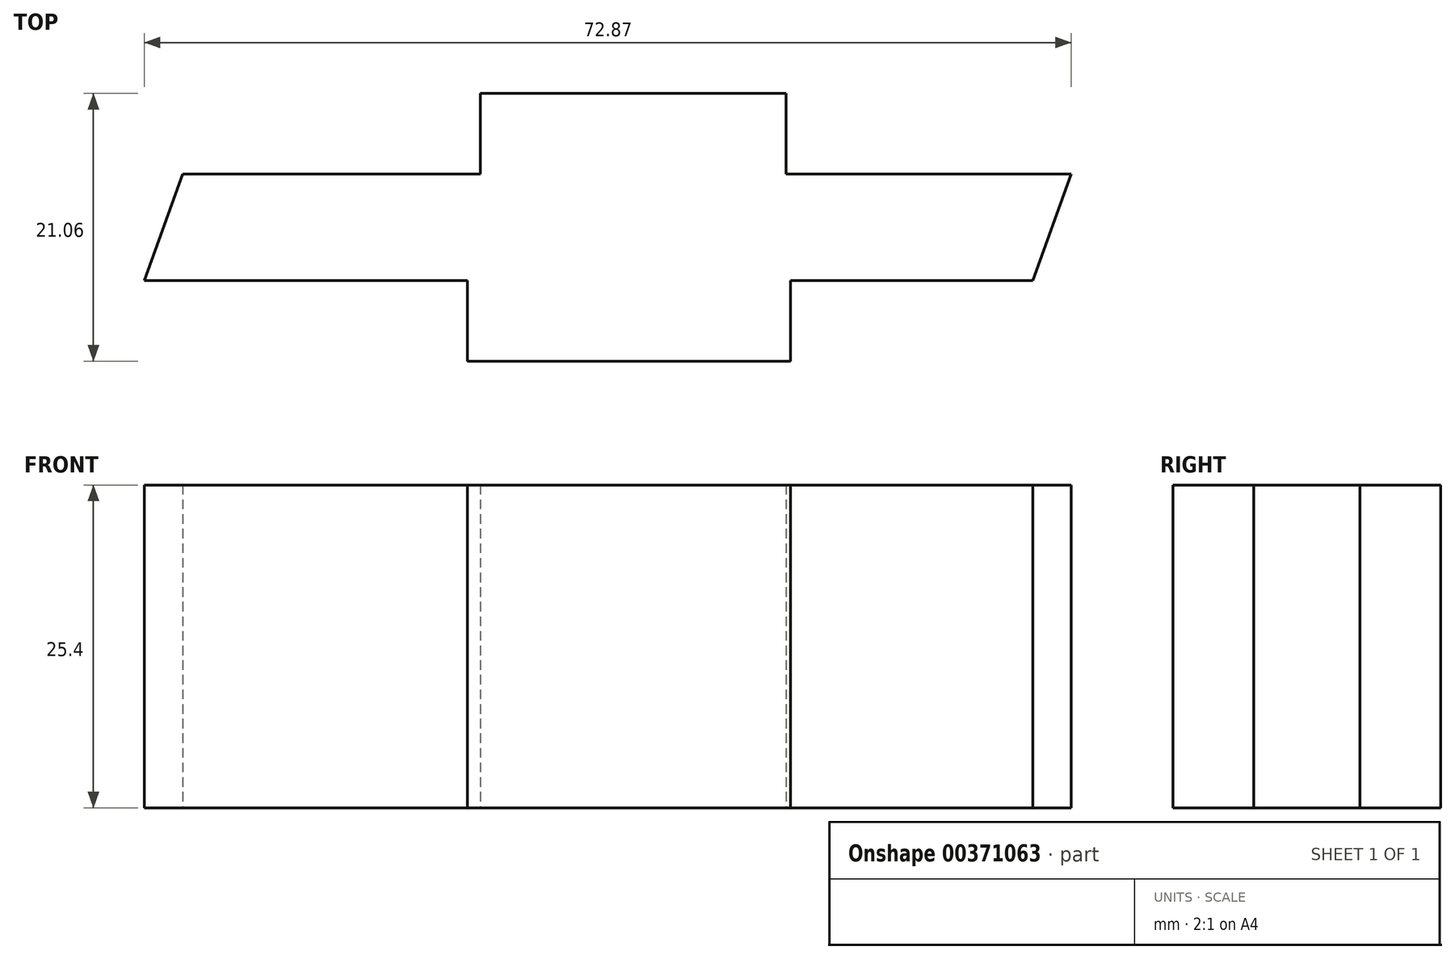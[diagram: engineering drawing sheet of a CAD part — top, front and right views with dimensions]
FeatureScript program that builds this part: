
annotation { "Feature Type Name" : "Feature", "Feature Type Description" : "" }
export const myFeature = defineFeature(function(context is Context, id is Id, definition is map)
    precondition{}
    {
        {
            var Q0;
            Q0=qCreatedBy(makeId("Top.planeOp"),FACE);
            var sketch = newSketch(context, id + "F0", { "sketchPlane" : qUnion([Q0])});
            skLineSegment(sketch, "E0", {"start": v(-22.5, 0) * mm, "end": v(2.9, 0) * mm});
            skLineSegment(sketch, "E1", {"start": v(2.9, 0) * mm, "end": v(2.9, 6.35) * mm});
            skLineSegment(sketch, "E2", {"start": v(2.9, 6.35) * mm, "end": v(21.95, 6.35) * mm});
            skLineSegment(sketch, "E3", {"start": v(-22.5, 0) * mm, "end": v(-22.5, 6.35) * mm});
            skLineSegment(sketch, "E4", {"start": v(-22.5, 6.35) * mm, "end": v(-47.9, 6.35) * mm});
            skLineSegment(sketch, "E5", {"start": v(21.95, 6.35) * mm, "end": v(24.97, 14.71) * mm});
            skLineSegment(sketch, "E6", {"start": v(24.97, 14.71) * mm, "end": v(2.56, 14.71) * mm});
            skLineSegment(sketch, "E7", {"start": v(2.56, 14.71) * mm, "end": v(2.56, 21.06) * mm});
            skLineSegment(sketch, "E8", {"start": v(2.56, 21.06) * mm, "end": v(-21.5, 21.06) * mm});
            skLineSegment(sketch, "E9", {"start": v(-21.5, 21.06) * mm, "end": v(-21.5, 14.71) * mm});
            skLineSegment(sketch, "E10", {"start": v(-47.9, 6.35) * mm, "end": v(-44.88, 14.71) * mm});
            skLineSegment(sketch, "E11", {"start": v(-44.88, 14.71) * mm, "end": v(-21.5, 14.71) * mm});
            skSolve(sketch);
        }
        {
            var Q0;
            Q0=makeQuery(id+"F0.imprint","IMPRINT",FACE,{"disambiguationData":[TD([[makeQuery(id+"F0.imprint","IMPRINT",EDGE,{"derivedFrom":sQuery(id+"F0.wireOp",EDGE,"E0")}),1.0]])]});
            extrude(context, id + "F1", {"entities" : qUnion([Q0]), "depth" : 25.4 * mm});
        }
    });
